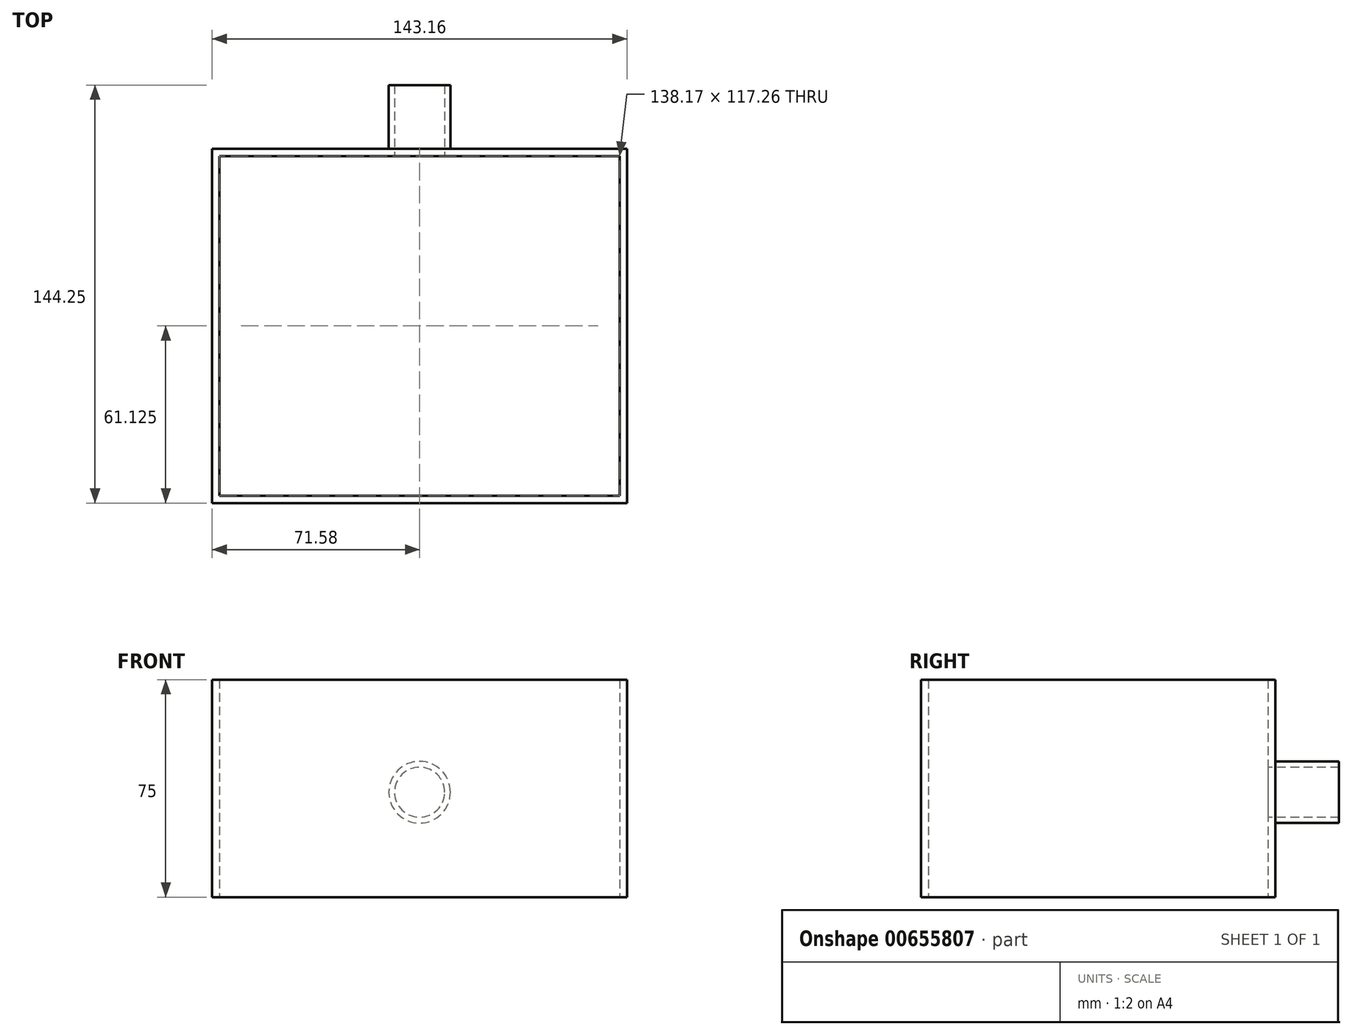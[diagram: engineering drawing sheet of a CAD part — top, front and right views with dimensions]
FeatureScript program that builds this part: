
annotation { "Feature Type Name" : "Feature", "Feature Type Description" : "" }
export const myFeature = defineFeature(function(context is Context, id is Id, definition is map)
    precondition{}
    {
        {
            var Q0;
            Q0=qCreatedBy(makeId("Top.planeOp"),FACE);
            var sketch = newSketch(context, id + "F0", { "sketchPlane" : qUnion([Q0])});
            skLineSegment(sketch, "E0.bottom", {"start": v(-71.58, 45.45) * mm, "end": v(71.58, 45.45) * mm});
            skLineSegment(sketch, "E0.top", {"start": v(-71.58, -51.8) * mm, "end": v(71.58, -51.8) * mm});
            skLineSegment(sketch, "E0.left", {"start": v(-71.58, 45.45) * mm, "end": v(-71.58, -51.8) * mm});
            skLineSegment(sketch, "E0.right", {"start": v(71.58, 45.45) * mm, "end": v(71.58, -51.8) * mm});
            skSolve(sketch);
        }
        {
            var Q0;
            Q0=makeQuery(id+"F0.imprint","IMPRINT",FACE,{"disambiguationData":[TD([[makeQuery(id+"F0.imprint","IMPRINT",EDGE,{"derivedFrom":sQuery(id+"F0.wireOp",EDGE,"E0.bottom")}),-1.0]])]});
            extrude(context, id + "F1", {"entities" : qUnion([Q0]), "depth" : 25 * mm, "offsetDistance" : 25 * mm});
        }
        {
            var Q0;
            Q0=makeQuery(id+"F1.opExtrude","SWEPT_FACE",FACE,{"disambiguationData":[OSD([sQuery(id+"F0.wireOp",EDGE,"E0.top")])]});
            var Q1;
            Q1=makeQuery(id+"F1.opExtrude","SWEPT_FACE",FACE,{"disambiguationData":[OSD([sQuery(id+"F0.wireOp",EDGE,"E0.bottom")])]});
            extrude(context, id + "F2", {"entities" : qUnion([Q0, Q1]), "operationType" : NewBodyOperationType.ADD, "depth" : 25 * mm, "offsetDistance" : 25 * mm});
        }
        {
            var Q0;
            {var subQ0=sQuery(id+"F0.wireOp",EDGE,"E0.top");Q0=makeQuery(id+"F2.boolean.opBoolean","MERGE",FACE,{"derivedFrom":[makeQuery(id+"F1.opExtrude","CAP_FACE",FACE,{"disambiguationData":[OSD([sQuery(id+"F0.wireOp",EDGE,"E0.bottom"),subQ0,sQuery(id+"F0.wireOp",EDGE,"E0.left"),sQuery(id+"F0.wireOp",EDGE,"E0.right")])],"isStart":false}),makeQuery(id+"F2.opExtrude","SWEPT_FACE",FACE,{"disambiguationData":[OSD([subQ0]),TDD([makeQuery(id+"F1.opExtrude","CAP_EDGE",EDGE,{"disambiguationData":[OSD([subQ0])],"isStart":false})])]})]});}
            var Q1;
            {var subQ0=sQuery(id+"F0.wireOp",EDGE,"E0.top");Q1=makeQuery(id+"F2.boolean.opBoolean","MERGE",FACE,{"derivedFrom":[makeQuery(id+"F1.opExtrude","CAP_FACE",FACE,{"disambiguationData":[OSD([sQuery(id+"F0.wireOp",EDGE,"E0.bottom"),subQ0,sQuery(id+"F0.wireOp",EDGE,"E0.left"),sQuery(id+"F0.wireOp",EDGE,"E0.right")])],"isStart":true}),makeQuery(id+"F2.opExtrude","SWEPT_FACE",FACE,{"disambiguationData":[OSD([subQ0]),TDD([makeQuery(id+"F1.opExtrude","CAP_EDGE",EDGE,{"disambiguationData":[OSD([subQ0])],"isStart":true})])]})]});}
            extrude(context, id + "F3", {"entities" : qUnion([Q0, Q1]), "operationType" : NewBodyOperationType.ADD, "depth" : 25 * mm, "offsetDistance" : 25 * mm});
        }
        {
            var Q0;
            {var subQ0=sQuery(id+"F0.wireOp",EDGE,"E0.top");var subQ1=sQuery(id+"F0.wireOp",EDGE,"E0.right");var subQ2=sQuery(id+"F0.wireOp",EDGE,"E0.left");var subQ3=sQuery(id+"F0.wireOp",EDGE,"E0.bottom");Q0=makeQuery(id+"F3.opExtrude","CAP_FACE",FACE,{"disambiguationData":[OSD([subQ3,subQ0,subQ2,subQ1]),TDD([makeQuery(id+"F2.boolean.opBoolean","MERGE",FACE,{"derivedFrom":[makeQuery(id+"F1.opExtrude","CAP_FACE",FACE,{"disambiguationData":[OSD([subQ3,subQ0,subQ2,subQ1])],"isStart":false}),makeQuery(id+"F2.opExtrude","SWEPT_FACE",FACE,{"disambiguationData":[OSD([subQ0]),TDD([makeQuery(id+"F1.opExtrude","CAP_EDGE",EDGE,{"disambiguationData":[OSD([subQ0])],"isStart":false})])]})]})])],"isStart":false});}
            var Q1;
            {var subQ0=sQuery(id+"F0.wireOp",EDGE,"E0.top");Q1=makeQuery(id+"F2.boolean.opBoolean","MERGE",FACE,{"derivedFrom":[makeQuery(id+"F1.opExtrude","CAP_FACE",FACE,{"disambiguationData":[OSD([sQuery(id+"F0.wireOp",EDGE,"E0.bottom"),subQ0,sQuery(id+"F0.wireOp",EDGE,"E0.left"),sQuery(id+"F0.wireOp",EDGE,"E0.right")])],"isStart":true}),makeQuery(id+"F2.opExtrude","SWEPT_FACE",FACE,{"disambiguationData":[OSD([subQ0]),TDD([makeQuery(id+"F1.opExtrude","CAP_EDGE",EDGE,{"disambiguationData":[OSD([subQ0])],"isStart":true})])]})]});}
            extrude(context, id + "F4", {"entities" : qUnion([Q0, Q1]), "operationType" : NewBodyOperationType.ADD, "depth" : 25 * mm, "offsetDistance" : 25 * mm});
        }
        {
            var Q0;
            {var subQ0=sQuery(id+"F0.wireOp",EDGE,"E0.top");Q0=makeQuery(id+"F2.boolean.opBoolean","MERGE",FACE,{"derivedFrom":[makeQuery(id+"F1.opExtrude","CAP_FACE",FACE,{"disambiguationData":[OSD([sQuery(id+"F0.wireOp",EDGE,"E0.bottom"),subQ0,sQuery(id+"F0.wireOp",EDGE,"E0.left"),sQuery(id+"F0.wireOp",EDGE,"E0.right")])],"isStart":true}),makeQuery(id+"F2.opExtrude","SWEPT_FACE",FACE,{"disambiguationData":[OSD([subQ0]),TDD([makeQuery(id+"F1.opExtrude","CAP_EDGE",EDGE,{"disambiguationData":[OSD([subQ0])],"isStart":true})])]})]});}
            var Q1;
            {var subQ0=sQuery(id+"F0.wireOp",EDGE,"E0.top");var subQ1=sQuery(id+"F0.wireOp",EDGE,"E0.right");var subQ2=sQuery(id+"F0.wireOp",EDGE,"E0.left");var subQ3=sQuery(id+"F0.wireOp",EDGE,"E0.bottom");Q1=makeQuery(id+"F4.opExtrude","CAP_FACE",FACE,{"disambiguationData":[OSD([subQ3,subQ0,subQ2,subQ1]),TDD([makeQuery(id+"F3.opExtrude","CAP_FACE",FACE,{"disambiguationData":[OSD([subQ3,subQ0,subQ2,subQ1]),TDD([makeQuery(id+"F2.boolean.opBoolean","MERGE",FACE,{"derivedFrom":[makeQuery(id+"F1.opExtrude","CAP_FACE",FACE,{"disambiguationData":[OSD([subQ3,subQ0,subQ2,subQ1])],"isStart":false}),makeQuery(id+"F2.opExtrude","SWEPT_FACE",FACE,{"disambiguationData":[OSD([subQ0]),TDD([makeQuery(id+"F1.opExtrude","CAP_EDGE",EDGE,{"disambiguationData":[OSD([subQ0])],"isStart":false})])]})]})])],"isStart":false})])],"isStart":false});}
            shell(context, id + "F5", {"entities" : qUnion([Q0, Q1]), "thickness" : 2.5 * mm});
        }
        {
            var Q0;
            {var subQ0=sQuery(id+"F0.wireOp",EDGE,"E0.bottom");var subQ1=makeQuery(id+"F1.opExtrude","CAP_EDGE",EDGE,{"disambiguationData":[OSD([subQ0])],"isStart":false});Q0=makeQuery(id+"F4.boolean.opBoolean","MERGE",FACE,{"derivedFrom":[makeQuery(id+"F3.boolean.opBoolean","MERGE",FACE,{"derivedFrom":[makeQuery(id+"F1.opExtrude","SWEPT_FACE",FACE,{"disambiguationData":[OSD([subQ0])]}),makeQuery(id+"F3.opExtrude","SWEPT_FACE",FACE,{"disambiguationData":[OSD([subQ0]),TDD([makeQuery(id+"F1.opExtrude","CAP_EDGE",EDGE,{"disambiguationData":[OSD([subQ0])],"isStart":true})])]}),makeQuery(id+"F3.opExtrude","SWEPT_FACE",FACE,{"disambiguationData":[OSD([subQ0]),TDD([subQ1])]})]}),makeQuery(id+"F4.opExtrude","SWEPT_FACE",FACE,{"disambiguationData":[OSD([subQ0]),TDD([makeQuery(id+"F3.opExtrude","CAP_EDGE",EDGE,{"disambiguationData":[OSD([subQ0]),TDD([subQ1])],"isStart":false})])]})]});}
            var sketch = newSketch(context, id + "F6", { "sketchPlane" : qUnion([Q0])});
            skCircle(sketch, "E1", {"center": v(0, 36.2) * mm, "radius": 10.64 * mm});
            skSolve(sketch);
        }
        {
            var Q0;
            Q0=makeQuery(id+"F6.imprint","IMPRINT",FACE,{"disambiguationData":[TD([[makeQuery(id+"F6.imprint","IMPRINT",EDGE,{"derivedFrom":sQuery(id+"F6.wireOp",EDGE,"E1")}),1.0]])]});
            extrude(context, id + "F7", {"entities" : qUnion([Q0]), "operationType" : NewBodyOperationType.ADD, "depth" : 22 * mm, "offsetDistance" : 25 * mm});
        }
        {
            var Q0;
            Q0=makeQuery(id+"F7.opExtrude","CAP_FACE",FACE,{"disambiguationData":[OSD([sQuery(id+"F6.wireOp",EDGE,"E1")])],"isStart":false});
            shell(context, id + "F8", {"entities" : qUnion([Q0]), "thickness" : 2 * mm});
        }
        {
            var Q0;
            Q0=makeQuery(id+"F8.opShell","OFFSET_FACE",FACE,{"disambiguationData":[OSD([sQuery(id+"F0.wireOp",EDGE,"E0.bottom")])]});
            extrude(context, id + "F9", {"entities" : qUnion([Q0]), "operationType" : NewBodyOperationType.REMOVE, "oppositeDirection" : true, "depth" : 25 * mm, "offsetDistance" : 25 * mm});
        }
    });
